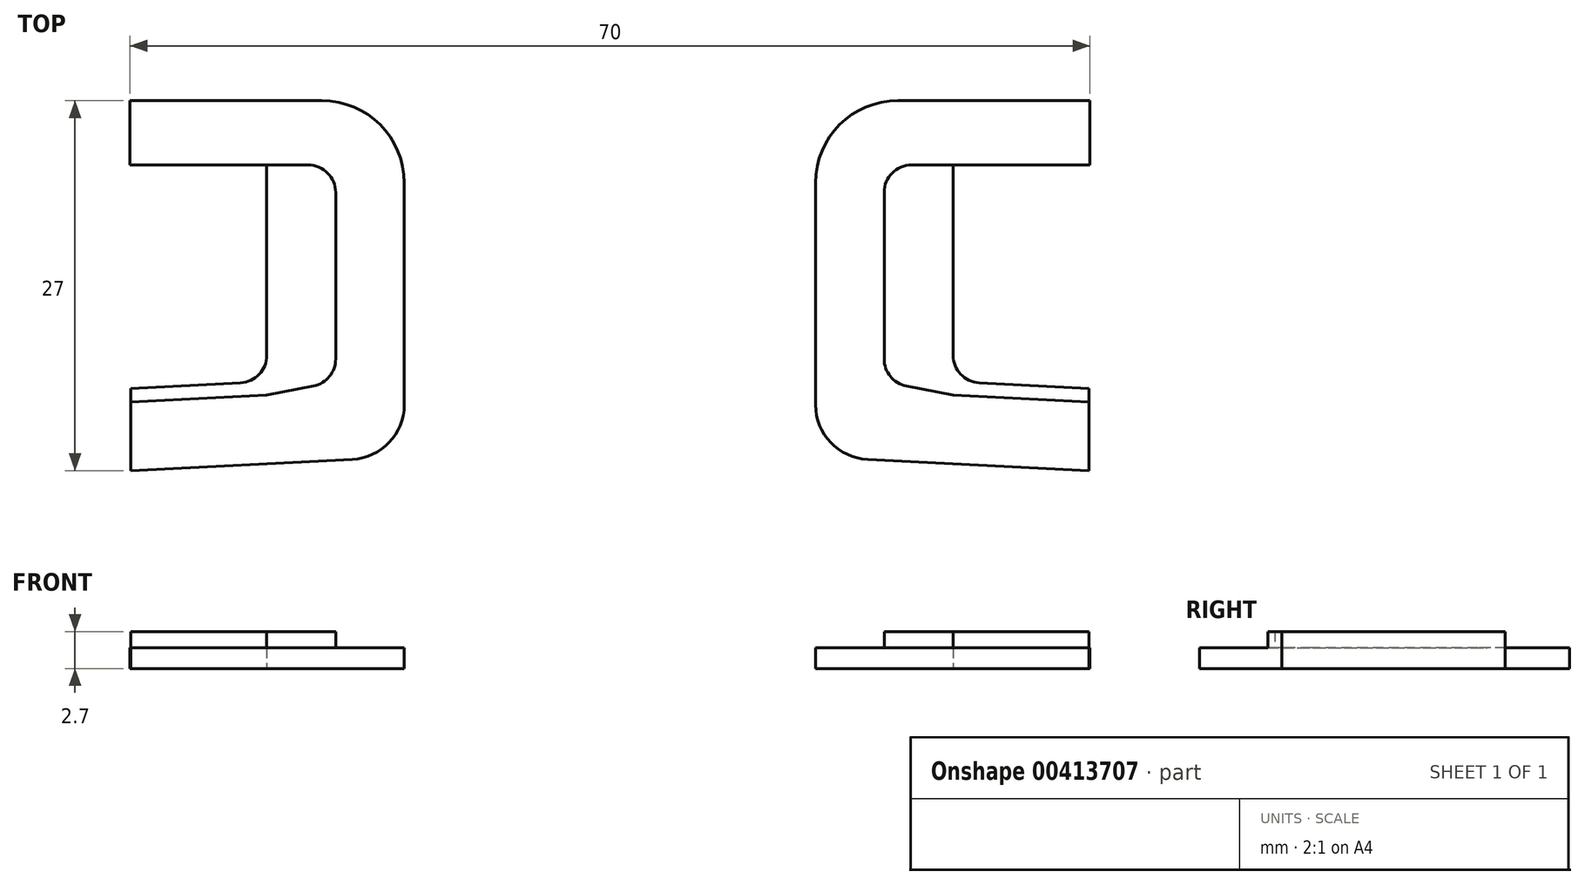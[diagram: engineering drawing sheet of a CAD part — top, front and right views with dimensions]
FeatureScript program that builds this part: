
annotation { "Feature Type Name" : "Feature", "Feature Type Description" : "" }
export const myFeature = defineFeature(function(context is Context, id is Id, definition is map)
    precondition{}
    {
        {
            var Q0;
            Q0=qCreatedBy(makeId("Top.planeOp"),FACE);
            var sketch = newSketch(context, id + "F0", { "sketchPlane" : qUnion([Q0])});
            skLineSegment(sketch, "E0", {"start": v(0, 0) * mm, "end": v(0, 26) * mm});
            skLineSegment(sketch, "E1", {"start": v(0, 26) * mm, "end": v(20, 26) * mm});
            skLineSegment(sketch, "E2", {"start": v(20, 26) * mm, "end": v(20, 21.3) * mm});
            skLineSegment(sketch, "E3", {"start": v(20, 21.3) * mm, "end": v(10.03, 21.3) * mm});
            skLineSegment(sketch, "E4", {"start": v(10.03, 21.3) * mm, "end": v(10.03, 5.5) * mm});
            skLineSegment(sketch, "E5", {"start": v(10.03, 5.5) * mm, "end": v(19.93, 5) * mm});
            skLineSegment(sketch, "E6", {"start": v(19.93, 5) * mm, "end": v(19.93, -1) * mm});
            skLineSegment(sketch, "E7", {"start": v(19.93, -1) * mm, "end": v(0, 0) * mm});
            skSolve(sketch);
        }
        {
            var Q0;
            Q0=makeQuery(id+"F0.imprint","IMPRINT",FACE,{"disambiguationData":[TD([[makeQuery(id+"F0.imprint","IMPRINT",EDGE,{"derivedFrom":sQuery(id+"F0.wireOp",EDGE,"E0")}),-1.0]])]});
            extrude(context, id + "F1", {"entities" : qUnion([Q0]), "depth" : 1.5 * mm});
        }
        {
            var Q0;
            Q0=makeQuery(id+"F1.opExtrude","SWEPT_EDGE",EDGE,{"disambiguationData":[OSD([sQuery(id+"F0.wireOp",EDGE,"E0"),sQuery(id+"F0.wireOp",EDGE,"E1")])]});
            fillet(context, id + "F2", {"entities" : qUnion([Q0]), "radius" : 6 * mm, "tangentPropagation" : true, "allowEdgeOverflow" : false});
        }
        {
            var Q0;
            Q0=makeQuery(id+"F1.opExtrude","SWEPT_EDGE",EDGE,{"disambiguationData":[OSD([sQuery(id+"F0.wireOp",EDGE,"E0"),sQuery(id+"F0.wireOp",EDGE,"E7")])]});
            fillet(context, id + "F3", {"entities" : qUnion([Q0]), "radius" : 4 * mm, "tangentPropagation" : true, "allowEdgeOverflow" : false});
        }
        {
            var Q0;
            Q0=makeQuery(id+"F1.opExtrude","CAP_FACE",FACE,{"disambiguationData":[OSD([sQuery(id+"F0.wireOp",EDGE,"E0"),sQuery(id+"F0.wireOp",EDGE,"E1"),sQuery(id+"F0.wireOp",EDGE,"E2"),sQuery(id+"F0.wireOp",EDGE,"E3"),sQuery(id+"F0.wireOp",EDGE,"E4"),sQuery(id+"F0.wireOp",EDGE,"E5"),sQuery(id+"F0.wireOp",EDGE,"E6"),sQuery(id+"F0.wireOp",EDGE,"E7")])],"isStart":false});
            var sketch = newSketch(context, id + "F4", { "sketchPlane" : qUnion([Q0])});
            skLineSegment(sketch, "E8", {"start": v(10.03, 21.3) * mm, "end": v(5, 21.3) * mm});
            skLineSegment(sketch, "E9", {"start": v(5, 21.3) * mm, "end": v(5, 5.5) * mm});
            skLineSegment(sketch, "E10", {"start": v(5, 5.5) * mm, "end": v(10.03, 4.5) * mm});
            skLineSegment(sketch, "E11", {"start": v(10.03, 4.5) * mm, "end": v(19.93, 4) * mm});
            skLineSegment(sketch, "E12", {"start": v(19.93, 4) * mm, "end": v(19.93, 5) * mm});
            skLineSegment(sketch, "E13", {"start": v(19.93, 5) * mm, "end": v(10.03, 5.5) * mm});
            skLineSegment(sketch, "E14", {"start": v(10.03, 5.5) * mm, "end": v(10.03, 21.3) * mm});
            skSolve(sketch);
        }
        {
            var Q0;
            Q0=makeQuery(id+"F4.imprint","IMPRINT",FACE,{"disambiguationData":[TD([[makeQuery(id+"F4.imprint","IMPRINT",EDGE,{"derivedFrom":sQuery(id+"F4.wireOp",EDGE,"E8")}),1.0]])]});
            extrude(context, id + "F5", {"entities" : qUnion([Q0]), "operationType" : NewBodyOperationType.ADD, "depth" : 1.2 * mm});
        }
        {
            var Q0;
            Q0=makeQuery(id+"F5.boolean.opBoolean","MERGE",EDGE,{"derivedFrom":[makeQuery(id+"F1.opExtrude","SWEPT_EDGE",EDGE,{"disambiguationData":[OSD([sQuery(id+"F0.wireOp",EDGE,"E4"),sQuery(id+"F0.wireOp",EDGE,"E5")])]}),makeQuery(id+"F5.opExtrude","SWEPT_EDGE",EDGE,{"disambiguationData":[OSD([sQuery(id+"F4.wireOp",EDGE,"E13"),sQuery(id+"F4.wireOp",EDGE,"E14")])]})]});
            var Q1;
            Q1=makeQuery(id+"F5.opExtrude","SWEPT_EDGE",EDGE,{"disambiguationData":[OSD([sQuery(id+"F4.wireOp",EDGE,"E8"),sQuery(id+"F4.wireOp",EDGE,"E9")])]});
            var Q2;
            Q2=makeQuery(id+"F5.opExtrude","SWEPT_EDGE",EDGE,{"disambiguationData":[OSD([sQuery(id+"F4.wireOp",EDGE,"E9"),sQuery(id+"F4.wireOp",EDGE,"E10")])]});
            fillet(context, id + "F6", {"entities" : qUnion([Q0, Q1, Q2]), "radius" : 2 * mm, "tangentPropagation" : true, "allowEdgeOverflow" : false});
        }
        {
            var Q0;
            Q0=makeQuery(id+"F1.opExtrude","SWEPT_BODY",BODY,{"disambiguationData":[OSD([sQuery(id+"F0.wireOp",EDGE,"E0"),sQuery(id+"F0.wireOp",EDGE,"E1"),sQuery(id+"F0.wireOp",EDGE,"E2"),sQuery(id+"F0.wireOp",EDGE,"E3"),sQuery(id+"F0.wireOp",EDGE,"E4"),sQuery(id+"F0.wireOp",EDGE,"E5"),sQuery(id+"F0.wireOp",EDGE,"E6"),sQuery(id+"F0.wireOp",EDGE,"E7")])]});
            transform(context, id + "F7", {"entities" : qUnion([Q0]), "transformType" : TransformType.TRANSLATION_3D, "dx" : 30 * mm, "dy" : 0 * mm, "dz" : 0 * mm, "makeCopy" : true});
        }
        {
            var Q0;
            Q0=makeQuery(id+"F7.opPattern","COPY",BODY,{"derivedFrom":makeQuery(id+"F1.opExtrude","SWEPT_BODY",BODY,{"disambiguationData":[OSD([sQuery(id+"F0.wireOp",EDGE,"E0"),sQuery(id+"F0.wireOp",EDGE,"E1"),sQuery(id+"F0.wireOp",EDGE,"E2"),sQuery(id+"F0.wireOp",EDGE,"E3"),sQuery(id+"F0.wireOp",EDGE,"E4"),sQuery(id+"F0.wireOp",EDGE,"E5"),sQuery(id+"F0.wireOp",EDGE,"E6"),sQuery(id+"F0.wireOp",EDGE,"E7")])]}),"instanceName":"1"});
            var Q1;
            Q1=qCreatedBy(makeId("Right.planeOp"),FACE);
            mirror(context, id + "F8", {"entities" : qUnion([Q0]), "mirrorPlane" : qUnion([Q1])});
        }
        {
            var Q0;
            Q0=makeQuery(id+"F7.opPattern","COPY",BODY,{"derivedFrom":makeQuery(id+"F1.opExtrude","SWEPT_BODY",BODY,{"disambiguationData":[OSD([sQuery(id+"F0.wireOp",EDGE,"E0"),sQuery(id+"F0.wireOp",EDGE,"E1"),sQuery(id+"F0.wireOp",EDGE,"E2"),sQuery(id+"F0.wireOp",EDGE,"E3"),sQuery(id+"F0.wireOp",EDGE,"E4"),sQuery(id+"F0.wireOp",EDGE,"E5"),sQuery(id+"F0.wireOp",EDGE,"E6"),sQuery(id+"F0.wireOp",EDGE,"E7")])]}),"instanceName":"1"});
            deleteBodies(context, id + "F9", {"entities" : qUnion([Q0])});
        }
    });
